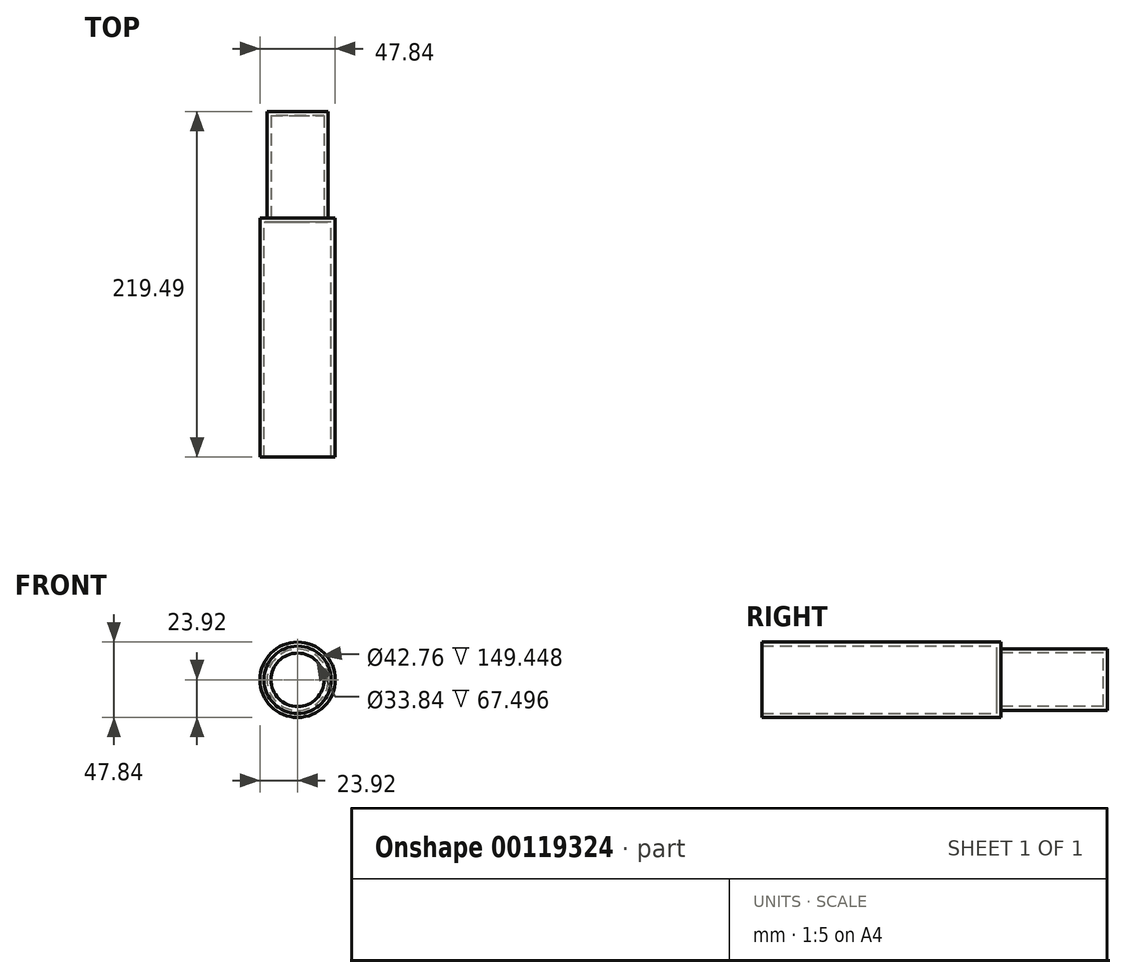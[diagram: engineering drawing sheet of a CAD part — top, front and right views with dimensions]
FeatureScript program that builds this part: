
annotation { "Feature Type Name" : "Feature", "Feature Type Description" : "" }
export const myFeature = defineFeature(function(context is Context, id is Id, definition is map)
    precondition{}
    {
        {
            var Q0;
            Q0=qCreatedBy(makeId("Front.planeOp"),FACE);
            var sketch = newSketch(context, id + "F0", { "sketchPlane" : qUnion([Q0])});
            skCircle(sketch, "E0", {"center": v(0, 0) * mm, "radius": 23.92 * mm});
            skSolve(sketch);
        }
        {
            var Q0;
            Q0=makeQuery(id+"F0.imprint","IMPRINT",FACE,{"disambiguationData":[TD([[makeQuery(id+"F0.imprint","IMPRINT",EDGE,{"derivedFrom":sQuery(id+"F0.wireOp",EDGE,"E0")}),1.0]])]});
            extrude(context, id + "F1", {"entities" : qUnion([Q0]), "depth" : 152 * mm});
        }
        {
            var Q0;
            Q0=makeQuery(id+"F1.opExtrude","CAP_FACE",FACE,{"disambiguationData":[OSD([sQuery(id+"F0.wireOp",EDGE,"E0")])],"isStart":false});
            var sketch = newSketch(context, id + "F2", { "sketchPlane" : qUnion([Q0])});
            skCircle(sketch, "E1", {"center": v(0, 0) * mm, "radius": 19.46 * mm});
            skSolve(sketch);
        }
        {
            var Q0;
            Q0=makeQuery(id+"F2.imprint","IMPRINT",FACE,{"disambiguationData":[TD([[makeQuery(id+"F2.imprint","IMPRINT",EDGE,{"derivedFrom":sQuery(id+"F2.wireOp",EDGE,"E1")}),1.0]])]});
            extrude(context, id + "F3", {"entities" : qUnion([Q0]), "operationType" : NewBodyOperationType.ADD, "oppositeDirection" : true, "depth" : 219.48 * mm});
        }
        {
            var Q0;
            Q0=makeQuery(id+"F1.opExtrude","CAP_FACE",FACE,{"disambiguationData":[OSD([sQuery(id+"F0.wireOp",EDGE,"E0")])],"isStart":false});
            shell(context, id + "F4", {"entities" : qUnion([Q0]), "thickness" : 2.54 * mm});
        }
    });
